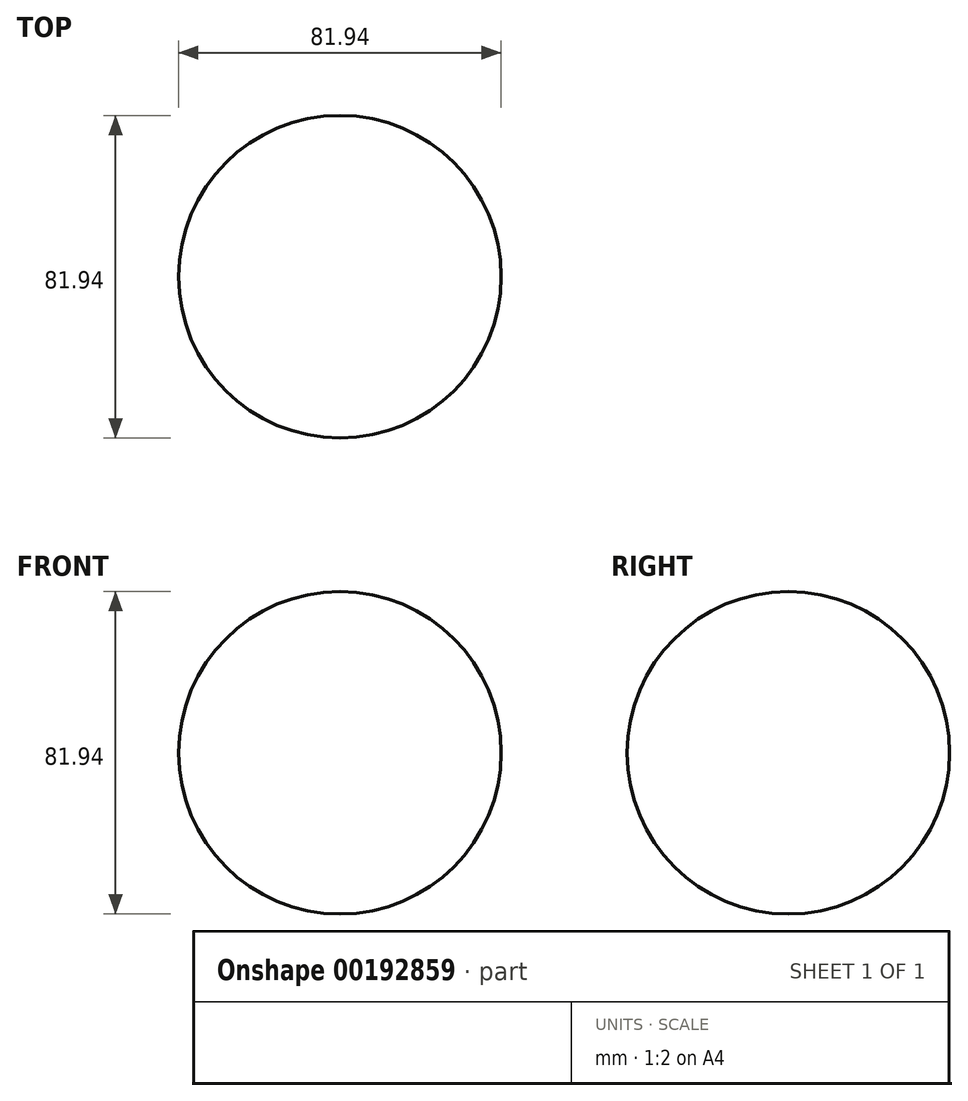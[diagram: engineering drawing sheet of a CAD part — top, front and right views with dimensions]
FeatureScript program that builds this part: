
annotation { "Feature Type Name" : "Feature", "Feature Type Description" : "" }
export const myFeature = defineFeature(function(context is Context, id is Id, definition is map)
    precondition{}
    {
        {
            var Q0;
            Q0=qCreatedBy(makeId("Front.planeOp"),FACE);
            var sketch = newSketch(context, id + "F0", { "sketchPlane" : qUnion([Q0])});
            skArc(sketch, "E0", {"start": v(40.97, 0) * mm, "mid": v(0, 40.97) * mm, "end": v(-40.97, 0) * mm});
            skLineSegment(sketch, "E1", {"start": v(-40.97, 0) * mm, "end": v(40.97, 0) * mm});
            skSolve(sketch);
        }
        {
            var Q0;
            Q0 = qSketchRegion(id + "F0", true);
            var Q1;
            Q1=sQuery(id+"F0.wireOp",EDGE,"E1");
            revolve(context, id + "F1", {"entities" : qUnion([Q0]), "axis" : qUnion([Q1]), "revolveType" : RevolveType.FULL});
        }
    });
